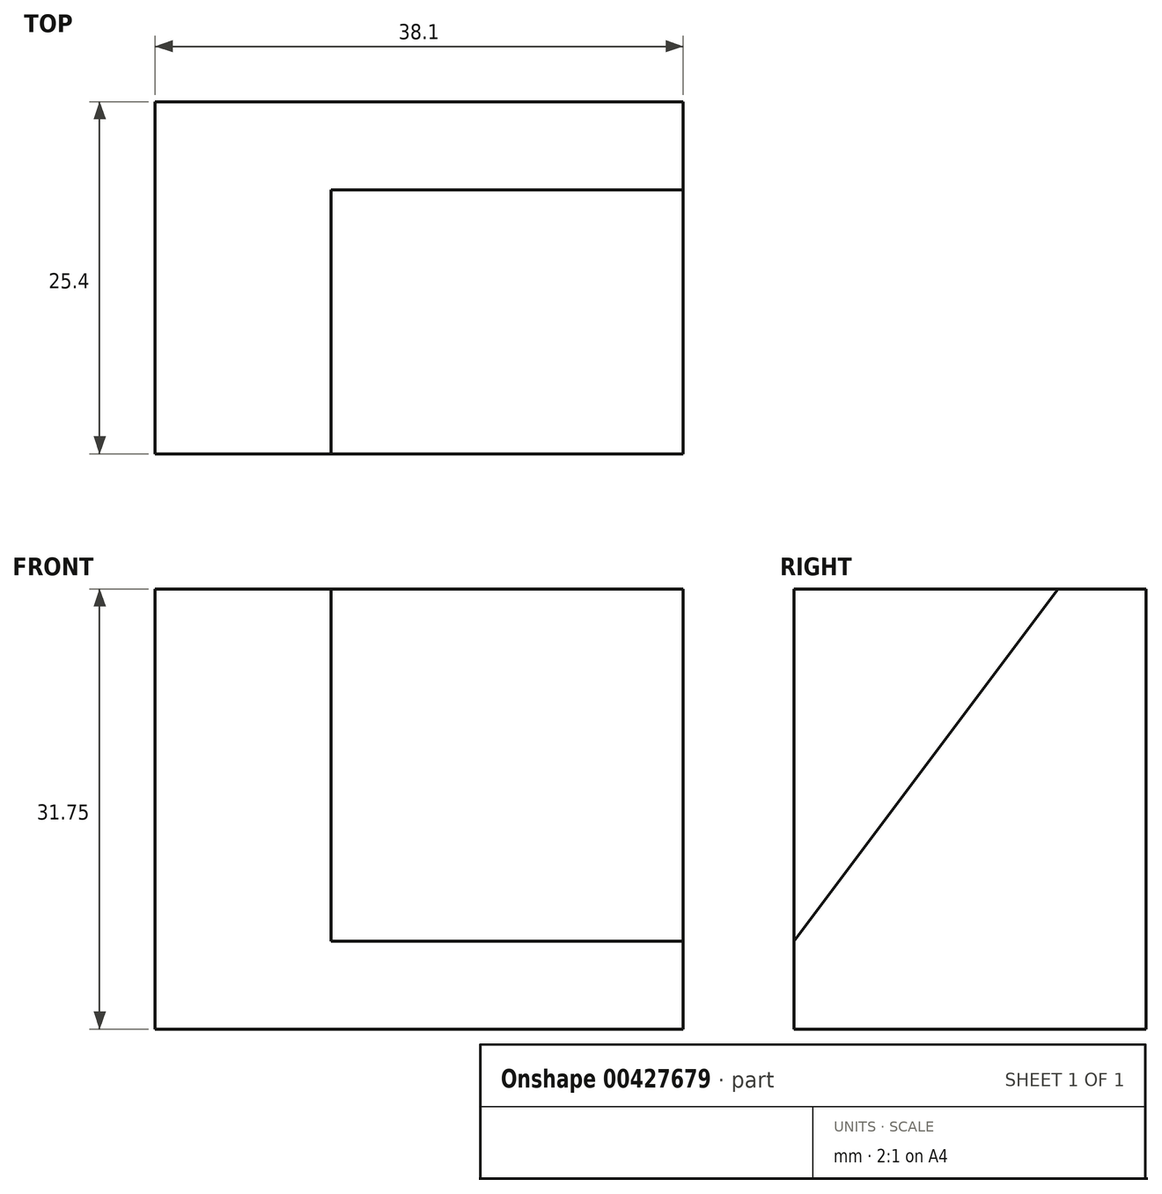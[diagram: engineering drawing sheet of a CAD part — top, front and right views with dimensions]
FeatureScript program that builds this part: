
annotation { "Feature Type Name" : "Feature", "Feature Type Description" : "" }
export const myFeature = defineFeature(function(context is Context, id is Id, definition is map)
    precondition{}
    {
        {
            var Q0;
            Q0=qCreatedBy(makeId("Top.planeOp"),FACE);
            var sketch = newSketch(context, id + "F0", { "sketchPlane" : qUnion([Q0])});
            skLineSegment(sketch, "E0", {"start": v(0, 0) * mm, "end": v(38.1, 0) * mm});
            skLineSegment(sketch, "E1", {"start": v(38.1, 0) * mm, "end": v(38.1, 25.4) * mm});
            skLineSegment(sketch, "E2", {"start": v(38.1, 25.4) * mm, "end": v(0, 25.4) * mm});
            skLineSegment(sketch, "E3", {"start": v(0, 25.4) * mm, "end": v(0, 0) * mm});
            skSolve(sketch);
        }
        {
            var Q0;
            Q0=makeQuery(id+"F0.imprint","IMPRINT",FACE,{"disambiguationData":[TD([[makeQuery(id+"F0.imprint","IMPRINT",EDGE,{"derivedFrom":sQuery(id+"F0.wireOp",EDGE,"E0")}),1.0]])]});
            extrude(context, id + "F1", {"entities" : qUnion([Q0]), "depth" : 31.75 * mm});
        }
        {
            var Q0;
            Q0=makeQuery(id+"F1.opExtrude","SWEPT_FACE",FACE,{"disambiguationData":[OSD([sQuery(id+"F0.wireOp",EDGE,"E1")])]});
            var sketch = newSketch(context, id + "F2", { "sketchPlane" : qUnion([Q0])});
            skLineSegment(sketch, "E4", {"start": v(19.05, 31.75) * mm, "end": v(0, 6.35) * mm});
            skLineSegment(sketch, "E5", {"start": v(0, 6.35) * mm, "end": v(0, 31.75) * mm});
            skLineSegment(sketch, "E6", {"start": v(0, 31.75) * mm, "end": v(19.05, 31.75) * mm});
            skSolve(sketch);
        }
        {
            var Q0;
            Q0=makeQuery(id+"F2.imprint","IMPRINT",FACE,{"disambiguationData":[TD([[makeQuery(id+"F2.imprint","IMPRINT",EDGE,{"derivedFrom":sQuery(id+"F2.wireOp",EDGE,"E4")}),-1.0]])]});
            extrude(context, id + "F3", {"entities" : qUnion([Q0]), "operationType" : NewBodyOperationType.REMOVE, "oppositeDirection" : true, "depth" : 25.4 * mm});
        }
    });
